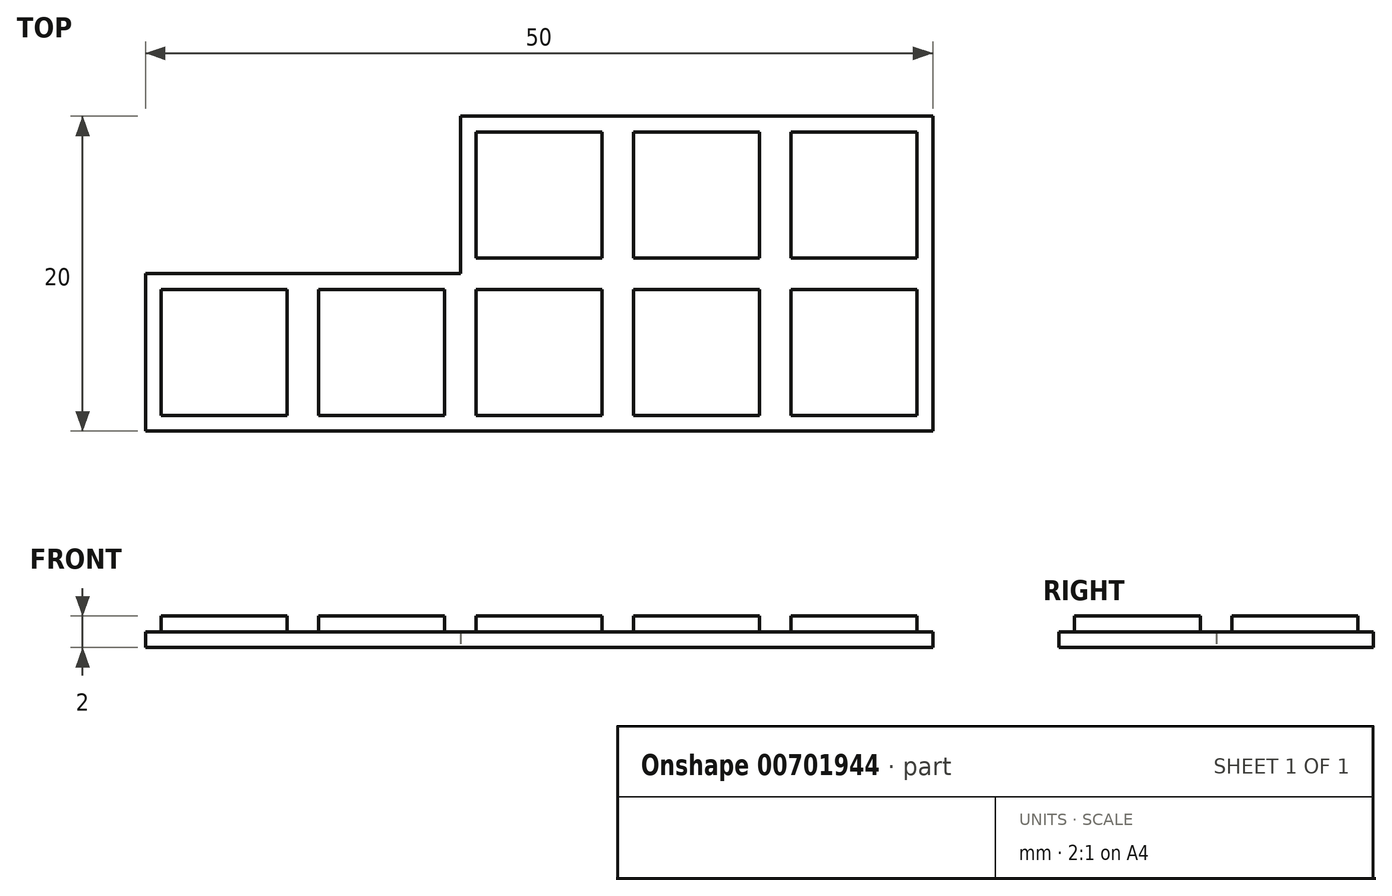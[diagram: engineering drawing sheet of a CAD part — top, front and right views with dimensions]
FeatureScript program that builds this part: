
annotation { "Feature Type Name" : "Feature", "Feature Type Description" : "" }
export const myFeature = defineFeature(function(context is Context, id is Id, definition is map)
    precondition{}
    {
        {
            var Q0;
            Q0=qCreatedBy(makeId("Top.planeOp"),FACE);
            var sketch = newSketch(context, id + "F0", { "sketchPlane" : qUnion([Q0])});
            skLineSegment(sketch, "E0", {"start": v(-23.65, 1.53) * mm, "end": v(-23.65, -8.47) * mm});
            skLineSegment(sketch, "E1", {"start": v(-23.65, -8.47) * mm, "end": v(26.35, -8.47) * mm});
            skLineSegment(sketch, "E2", {"start": v(26.35, -8.47) * mm, "end": v(26.35, 11.53) * mm});
            skLineSegment(sketch, "E3", {"start": v(26.35, 11.53) * mm, "end": v(-3.65, 11.53) * mm});
            skLineSegment(sketch, "E4", {"start": v(-3.65, 11.53) * mm, "end": v(-3.65, 1.53) * mm});
            skLineSegment(sketch, "E5", {"start": v(-3.65, 1.53) * mm, "end": v(-23.65, 1.53) * mm});
            skSolve(sketch);
        }
        {
            var Q0;
            Q0=makeQuery(id+"F0.imprint","IMPRINT",FACE,{"disambiguationData":[TD([[makeQuery(id+"F0.imprint","IMPRINT",EDGE,{"derivedFrom":sQuery(id+"F0.wireOp",EDGE,"qFyTJhzL-X8oy-V4Zn-n2UO-jb0vi0Htoton")}),1.0]])]});
            var Q1;
            Q1=makeQuery(id+"F0.imprint","IMPRINT",FACE,{"disambiguationData":[TD([[makeQuery(id+"F0.imprint","IMPRINT",EDGE,{"derivedFrom":sQuery(id+"F0.wireOp",EDGE,"8X8TdU3l-BQ1k-w8db-zCfl-hLHWanO2PYAS")}),1.0]])]});
            var Q2;
            Q2=makeQuery(id+"F0.imprint","IMPRINT",FACE,{"disambiguationData":[TD([[makeQuery(id+"F0.imprint","IMPRINT",EDGE,{"derivedFrom":sQuery(id+"F0.wireOp",EDGE,"E0")}),1.0]])]});
            var Q3;
            Q3=makeQuery(id+"F0.imprint","IMPRINT",FACE,{"disambiguationData":[TD([[makeQuery(id+"F0.imprint","IMPRINT",EDGE,{"derivedFrom":sQuery(id+"F0.wireOp",EDGE,"Ld2wisXk-MDIs-XWBZ-cWGf-ZvUSmQWxL9CZ")}),1.0]])]});
            extrude(context, id + "F1", {"entities" : qUnion([Q0, Q1, Q2, Q3]), "depth" : 1 * mm, "offsetDistance" : 25 * mm});
        }
        {
            var Q0;
            Q0=makeQuery(id+"F1.opExtrude","CAP_FACE",FACE,{"disambiguationData":[OSD([sQuery(id+"F0.wireOp",EDGE,"E0"),sQuery(id+"F0.wireOp",EDGE,"E1"),sQuery(id+"F0.wireOp",EDGE,"E2"),sQuery(id+"F0.wireOp",EDGE,"E3"),sQuery(id+"F0.wireOp",EDGE,"E4"),sQuery(id+"F0.wireOp",EDGE,"E5")])],"isStart":false});
            var sketch = newSketch(context, id + "F2", { "sketchPlane" : qUnion([Q0])});
            skLineSegment(sketch, "E6", {"start": v(-23.65, 0.53) * mm, "end": v(26.35, 0.53) * mm});
            skLineSegment(sketch, "E7", {"start": v(-2.65, 11.53) * mm, "end": v(-2.65, -8.47) * mm});
            skLineSegment(sketch, "E8", {"start": v(-23.65, -7.47) * mm, "end": v(26.35, -7.47) * mm});
            skLineSegment(sketch, "E9", {"start": v(-3.65, 10.53) * mm, "end": v(26.35, 10.53) * mm});
            skLineSegment(sketch, "E10", {"start": v(25.35, 11.53) * mm, "end": v(25.35, -8.47) * mm});
            skLineSegment(sketch, "E11", {"start": v(-22.65, 1.53) * mm, "end": v(-22.65, -8.47) * mm});
            skLineSegment(sketch, "E12", {"start": v(-3.65, 1.53) * mm, "end": v(26.35, 1.53) * mm, "construction": true});
            skLineSegment(sketch, "E13", {"start": v(-3.65, 1.53) * mm, "end": v(-3.65, -8.47) * mm, "construction": true});
            skLineSegment(sketch, "E14", {"start": v(-13.65, 1.53) * mm, "end": v(-13.65, -8.47) * mm, "construction": true});
            skLineSegment(sketch, "E15", {"start": v(16.35, 11.53) * mm, "end": v(16.35, -8.47) * mm, "construction": true});
            skLineSegment(sketch, "E16", {"start": v(6.35, 11.53) * mm, "end": v(6.35, -8.47) * mm, "construction": true});
            skLineSegment(sketch, "E17", {"start": v(-3.65, 2.53) * mm, "end": v(26.35, 2.53) * mm});
            skLineSegment(sketch, "E18", {"start": v(-14.65, 1.53) * mm, "end": v(-14.65, -8.47) * mm});
            skLineSegment(sketch, "E19", {"start": v(-12.65, 1.53) * mm, "end": v(-12.65, -8.47) * mm});
            skLineSegment(sketch, "E20", {"start": v(-4.65, 1.53) * mm, "end": v(-4.65, -8.47) * mm});
            skLineSegment(sketch, "E21", {"start": v(5.35, 11.53) * mm, "end": v(5.35, -8.47) * mm});
            skLineSegment(sketch, "E22", {"start": v(7.35, 11.53) * mm, "end": v(7.35, -8.47) * mm});
            skLineSegment(sketch, "E23", {"start": v(15.35, 11.53) * mm, "end": v(15.35, -8.47) * mm});
            skLineSegment(sketch, "E24", {"start": v(17.35, 11.53) * mm, "end": v(17.35, -8.47) * mm});
            skSolve(sketch);
        }
        {
            var Q0;
            {var subQ0=sQuery(id+"F2.wireOp",EDGE,"E11");var subQ1=sQuery(id+"F2.wireOp",EDGE,"E6");var subQ2=makeQuery(id+"F2.imprint","INTERSECT",VERTEX,{"derivedFrom":[subQ1,subQ0]});Q0=makeQuery(id+"F2.imprint","IMPRINT",FACE,{"disambiguationData":[TD([[makeQuery(id+"F2.imprint","IMPRINT",EDGE,{"disambiguationData":[TD([[subQ2,-1.0]])],"derivedFrom":subQ1}),-1.0]])]});}
            var Q1;
            {var subQ0=sQuery(id+"F2.wireOp",EDGE,"E19");var subQ1=sQuery(id+"F2.wireOp",EDGE,"E6");var subQ2=makeQuery(id+"F2.imprint","INTERSECT",VERTEX,{"derivedFrom":[subQ1,subQ0]});Q1=makeQuery(id+"F2.imprint","IMPRINT",FACE,{"disambiguationData":[TD([[makeQuery(id+"F2.imprint","IMPRINT",EDGE,{"disambiguationData":[TD([[subQ2,-1.0]])],"derivedFrom":subQ1}),-1.0]])]});}
            var Q2;
            {var subQ0=sQuery(id+"F2.wireOp",EDGE,"E9");var subQ1=sQuery(id+"F2.wireOp",EDGE,"E7");var subQ2=makeQuery(id+"F2.imprint","INTERSECT",VERTEX,{"derivedFrom":[subQ1,subQ0]});Q2=makeQuery(id+"F2.imprint","IMPRINT",FACE,{"disambiguationData":[TD([[makeQuery(id+"F2.imprint","IMPRINT",EDGE,{"disambiguationData":[TD([[subQ2,-1.0]])],"derivedFrom":subQ1}),1.0]])]});}
            var Q3;
            {var subQ0=sQuery(id+"F2.wireOp",EDGE,"E22");var subQ1=sQuery(id+"F2.wireOp",EDGE,"E9");var subQ2=makeQuery(id+"F2.imprint","INTERSECT",VERTEX,{"derivedFrom":[subQ1,subQ0]});Q3=makeQuery(id+"F2.imprint","IMPRINT",FACE,{"disambiguationData":[TD([[makeQuery(id+"F2.imprint","IMPRINT",EDGE,{"disambiguationData":[TD([[subQ2,-1.0]])],"derivedFrom":subQ1}),-1.0]])]});}
            var Q4;
            {var subQ0=sQuery(id+"F2.wireOp",EDGE,"E22");var subQ1=sQuery(id+"F2.wireOp",EDGE,"E6");var subQ2=makeQuery(id+"F2.imprint","INTERSECT",VERTEX,{"derivedFrom":[subQ1,subQ0]});Q4=makeQuery(id+"F2.imprint","IMPRINT",FACE,{"disambiguationData":[TD([[makeQuery(id+"F2.imprint","IMPRINT",EDGE,{"disambiguationData":[TD([[subQ2,-1.0]])],"derivedFrom":subQ1}),-1.0]])]});}
            var Q5;
            {var subQ0=sQuery(id+"F2.wireOp",EDGE,"E24");var subQ1=sQuery(id+"F2.wireOp",EDGE,"E6");var subQ2=makeQuery(id+"F2.imprint","INTERSECT",VERTEX,{"derivedFrom":[subQ1,subQ0]});Q5=makeQuery(id+"F2.imprint","IMPRINT",FACE,{"disambiguationData":[TD([[makeQuery(id+"F2.imprint","IMPRINT",EDGE,{"disambiguationData":[TD([[subQ2,-1.0]])],"derivedFrom":subQ1}),-1.0]])]});}
            var Q6;
            {var subQ0=sQuery(id+"F2.wireOp",EDGE,"E24");var subQ1=sQuery(id+"F2.wireOp",EDGE,"E9");var subQ2=makeQuery(id+"F2.imprint","INTERSECT",VERTEX,{"derivedFrom":[subQ1,subQ0]});Q6=makeQuery(id+"F2.imprint","IMPRINT",FACE,{"disambiguationData":[TD([[makeQuery(id+"F2.imprint","IMPRINT",EDGE,{"disambiguationData":[TD([[subQ2,-1.0]])],"derivedFrom":subQ1}),-1.0]])]});}
            var Q7;
            {var subQ0=sQuery(id+"F2.wireOp",EDGE,"E7");var subQ1=sQuery(id+"F2.wireOp",EDGE,"E6");var subQ2=makeQuery(id+"F2.imprint","INTERSECT",VERTEX,{"derivedFrom":[subQ1,subQ0]});Q7=makeQuery(id+"F2.imprint","IMPRINT",FACE,{"disambiguationData":[TD([[makeQuery(id+"F2.imprint","IMPRINT",EDGE,{"disambiguationData":[TD([[subQ2,-1.0]])],"derivedFrom":subQ1}),-1.0]])]});}
            extrude(context, id + "F3", {"entities" : qUnion([Q0, Q1, Q2, Q3, Q4, Q5, Q6, Q7]), "operationType" : NewBodyOperationType.ADD, "depth" : 1 * mm, "offsetDistance" : 25 * mm});
        }
    });
